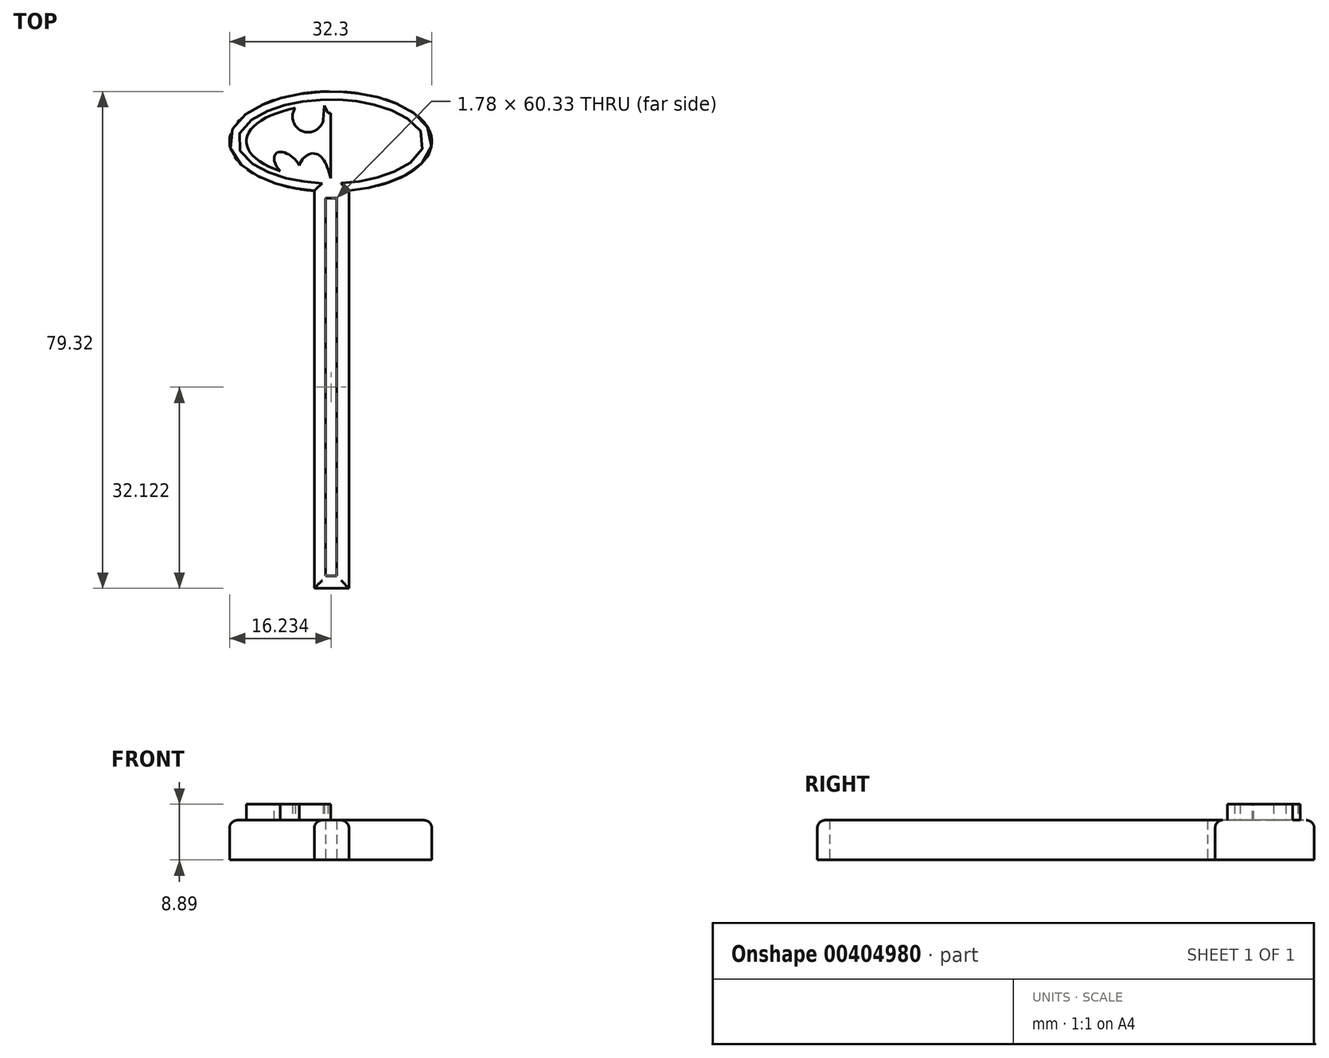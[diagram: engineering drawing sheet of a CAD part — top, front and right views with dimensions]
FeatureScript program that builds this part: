
annotation { "Feature Type Name" : "Feature", "Feature Type Description" : "" }
export const myFeature = defineFeature(function(context is Context, id is Id, definition is map)
    precondition{}
    {
        {
            var Q0;
            Q0=qCreatedBy(makeId("Top.planeOp"),FACE);
            var sketch = newSketch(context, id + "F0", { "sketchPlane" : qUnion([Q0])});
            skLineSegment(sketch, "E0.bottom", {"start": v(-8.05, 29.3) * mm, "end": v(-6.28, 29.3) * mm});
            skLineSegment(sketch, "E0.top", {"start": v(-8.05, -31.02) * mm, "end": v(-6.28, -31.02) * mm});
            skLineSegment(sketch, "E0.left", {"start": v(-8.05, 29.3) * mm, "end": v(-8.05, -31.02) * mm});
            skLineSegment(sketch, "E0.right", {"start": v(-6.28, 29.3) * mm, "end": v(-6.28, -31.02) * mm});
            skLineSegment(sketch, "E1.top", {"start": v(-9.87, -32.98) * mm, "end": v(-4.33, -32.98) * mm});
            skLineSegment(sketch, "E1.left", {"start": v(-9.87, 30.52) * mm, "end": v(-9.87, -32.98) * mm});
            skLineSegment(sketch, "E1.right", {"start": v(-4.33, 30.52) * mm, "end": v(-4.33, -32.98) * mm});
            skEllipticalArc(sketch, "E2", {});
            skPoint(sketch, "E3.startSnap0", {"position": v(-7.25, 46.34) * mm});
            skPoint(sketch, "E3.start.orphan", {"position": v(-7.25, 51.5) * mm});
            const initialGuessF0  = {"E2": [-0.007252356503158808, 0.03836836293339729, 1, 0, 0.016150043811649084, 0.007975973144719452, 4.894343702648654, 4.54976842266986]};
            skSetInitialGuess(sketch, initialGuessF0);
            skSolve(sketch);
        }
        {
            var Q0;
            Q0=qSketchRegion(id+"F0",true);
            extrude(context, id + "F1", {"entities" : qUnion([Q0]), "depth" : 6.35 * mm});
        }
        {
            var Q0;
            Q0=makeQuery(id+"F1.opExtrude","CAP_FACE",FACE,{"disambiguationData":[OSD([sQuery(id+"F0.wireOp",EDGE,"E0.bottom"),sQuery(id+"F0.wireOp",EDGE,"E0.top"),sQuery(id+"F0.wireOp",EDGE,"E0.left"),sQuery(id+"F0.wireOp",EDGE,"E0.right"),sQuery(id+"F0.wireOp",EDGE,"E1.top"),sQuery(id+"F0.wireOp",EDGE,"E1.left"),sQuery(id+"F0.wireOp",EDGE,"E1.right"),sQuery(id+"F0.wireOp",EDGE,"E2")])],"isStart":false});
            var sketch = newSketch(context, id + "F2", { "sketchPlane" : qUnion([Q0])});
            skEllipticalArc(sketch, "E4", {});
            skLineSegment(sketch, "E5", {"start": v(-7.25, 48.68) * mm, "end": v(-7.25, 32.47) * mm});
            skPoint(sketch, "E5.endSnap0", {"position": v(-7.25, 30.4) * mm});
            skLineSegment(sketch, "E6", {"start": v(-7.25, 42.88) * mm, "end": v(-6.79, 42.88) * mm});
            skPoint(sketch, "E7.first.point", {"position": v(-5.08, 42) * mm});
            skPoint(sketch, "E7.second.point", {"position": v(-1.6, 43.72) * mm});
            skPoint(sketch, "E7.third.point", {"position": v(-3.3, 39.92) * mm});
            skEllipticalArc(sketch, "E8", {});
            skFitSpline(sketch, "E9", {"points": [v(-7.25, 32.47) * mm, v(-4.78, 36.44) * mm, v(-2.26, 34.55) * mm], "startDerivative": vector(2.36, 11.13) * mm, "endDerivative": vector(2.41, -8.56) * mm});
            skEllipticalArc(sketch, "E10.trimOffspring", {});
            skPoint(sketch, "E11.trimOffspring.end.orphan", {"position": v(-7.25, 29.75) * mm});
            skLineSegment(sketch, "E12.MirrorCS", {"start": v(-7.25, 42.88) * mm, "end": v(-7.72, 42.88) * mm});
            skEllipticalArc(sketch, "E13.MirrorCS", {});
            skFitSpline(sketch, "E14.MirrorCS", {"points": [v(-7.25, 32.47) * mm, v(-9.73, 36.44) * mm, v(-12.25, 34.55) * mm], "startDerivative": vector(-2.36, 11.13) * mm, "endDerivative": vector(-2.41, -8.56) * mm});
            skLineSegment(sketch, "E15", {"start": v(-6.79, 42.88) * mm, "end": v(-6.26, 44.13) * mm});
            skLineSegment(sketch, "E16", {"start": v(-6.26, 44.13) * mm, "end": v(-6.07, 41.8) * mm});
            skArc(sketch, "E17", {"start": v(-6.07, 41.8) * mm, "mid": v(-2.67, 40.04) * mm, "end": v(-1.6, 43.72) * mm});
            skPoint(sketch, "E17.third.point", {"position": v(-2.29, 40.25) * mm});
            skLineSegment(sketch, "E18.MirrorCS", {"start": v(-7.72, 42.88) * mm, "end": v(-8.25, 44.13) * mm});
            skLineSegment(sketch, "E19.MirrorCS", {"start": v(-8.25, 44.13) * mm, "end": v(-8.43, 41.8) * mm});
            skArc(sketch, "E20.MirrorCS", {"start": v(-8.43, 41.8) * mm, "mid": v(-11.83, 40.04) * mm, "end": v(-12.9, 43.72) * mm});
            const initialGuessF2  = {"E4": [-0.007252356503158808, 0.03836836293339729, 1, 0, 0.013452716371891214, 0.0058950630208120984, 5.355480264337791, 1.137223244960225], "E8": [-0.00042749958811327815, 0.03451338782906532, 0.7071070265716229, 0.7071065358013869, 0.002727908301320936, 0.0014921496315674547, 4.811673716025654, 2.054311453161399], "E10.trimOffspring": [-0.007252356503158808, 0.03836836293339729, 1, 0, 0.013452716371891214, 0.0058950630208120984, 2.0043694086295685, 4.069297696431589], "E13.MirrorCS": [-0.014078464221015828, 0.034509578750198666, -0.7071070265716227, 0.7071065358013872, 0.002727908301320936, 0.0014921496315674547, 4.228873854018188, 1.4715115911539325]};
            skSetInitialGuess(sketch, initialGuessF2);
            skSolve(sketch);
        }
        {
            var Q0;
            Q0=qSketchRegion(id+"F2",true);
            extrude(context, id + "F3", {"entities" : qUnion([Q0]), "depth" : 2.54 * mm});
        }
        {
            var Q0;
            Q0=makeQuery(id+"F1.opExtrude","CAP_EDGE",EDGE,{"disambiguationData":[OSD([sQuery(id+"F0.wireOp",EDGE,"E2")])],"isStart":false});
            fillet(context, id + "F4", {"entities" : qUnion([Q0]), "radius" : 1.27 * mm, "tangentPropagation" : true, "allowEdgeOverflow" : false});
        }
        {
            var Q0;
            Q0=makeQuery(id+"F1.opExtrude","CAP_EDGE",EDGE,{"disambiguationData":[OSD([sQuery(id+"F0.wireOp",EDGE,"E1.right")])],"isStart":false});
            var Q1;
            Q1=makeQuery(id+"F1.opExtrude","CAP_EDGE",EDGE,{"disambiguationData":[OSD([sQuery(id+"F0.wireOp",EDGE,"E1.left")])],"isStart":false});
            var Q2;
            Q2=makeQuery(id+"F1.opExtrude","CAP_EDGE",EDGE,{"disambiguationData":[OSD([sQuery(id+"F0.wireOp",EDGE,"E1.top")])],"isStart":false});
            fillet(context, id + "F5", {"entities" : qUnion([Q0, Q1, Q2]), "radius" : 1.27 * mm, "tangentPropagation" : true, "allowEdgeOverflow" : false});
        }
    });
